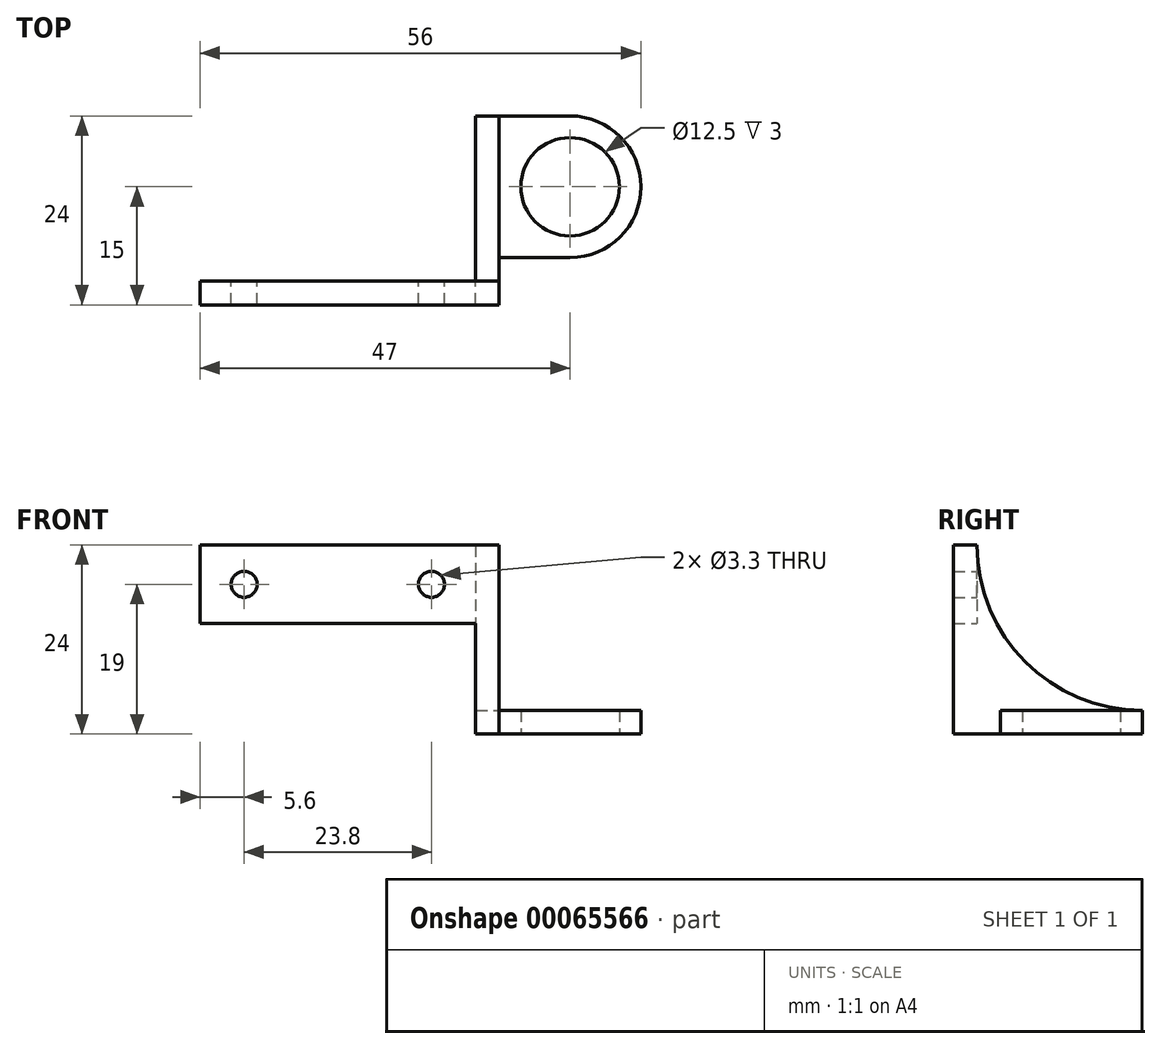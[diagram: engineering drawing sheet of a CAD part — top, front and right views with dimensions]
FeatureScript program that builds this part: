
annotation { "Feature Type Name" : "Feature", "Feature Type Description" : "" }
export const myFeature = defineFeature(function(context is Context, id is Id, definition is map)
    precondition{}
    {
        {
            var Q0;
            Q0=qCreatedBy(makeId("Front.planeOp"),FACE);
            var sketch = newSketch(context, id + "F0", { "sketchPlane" : qUnion([Q0])});
            skLineSegment(sketch, "E0.bottom", {"start": v(-17.5, 5) * mm, "end": v(17.5, 5) * mm});
            skLineSegment(sketch, "E0.top", {"start": v(-17.5, -5) * mm, "end": v(17.5, -5) * mm});
            skLineSegment(sketch, "E0.left", {"start": v(-17.5, 5) * mm, "end": v(-17.5, -5) * mm});
            skLineSegment(sketch, "E0.right", {"start": v(17.5, 5) * mm, "end": v(17.5, -5) * mm});
            skCircle(sketch, "E1", {"center": v(-11.9, 0) * mm, "radius": 1.65 * mm});
            skCircle(sketch, "E2", {"center": v(11.9, 0) * mm, "radius": 1.65 * mm});
            skSolve(sketch);
        }
        {
            var Q0;
            Q0=makeQuery(id+"F0.imprint","IMPRINT",FACE,{"disambiguationData":[TD([[makeQuery(id+"F0.imprint","IMPRINT",EDGE,{"derivedFrom":sQuery(id+"F0.wireOp",EDGE,"E0.bottom")}),-1.0]])]});
            extrude(context, id + "F1", {"entities" : qUnion([Q0]), "depth" : 3 * mm});
        }
        {
            var Q0;
            Q0=makeQuery(id+"F1.opExtrude","SWEPT_FACE",FACE,{"disambiguationData":[OSD([sQuery(id+"F0.wireOp",EDGE,"E0.right")])]});
            var sketch = newSketch(context, id + "F2", { "sketchPlane" : qUnion([Q0])});
            skLineSegment(sketch, "E3.bottom", {"start": v(-3, 5) * mm, "end": v(21, 5) * mm});
            skLineSegment(sketch, "E3.top", {"start": v(-3, -19) * mm, "end": v(21, -19) * mm});
            skLineSegment(sketch, "E3.left", {"start": v(-3, 5) * mm, "end": v(-3, -19) * mm});
            skLineSegment(sketch, "E3.right", {"start": v(21, 5) * mm, "end": v(21, -19) * mm});
            skSolve(sketch);
        }
        {
            var Q0;
            Q0 = qSketchRegion(id + "F2", true);
            extrude(context, id + "F3", {"entities" : qUnion([Q0]), "operationType" : NewBodyOperationType.ADD, "depth" : 3 * mm});
        }
        {
            var Q0;
            Q0=makeQuery(id+"F3.opExtrude","SWEPT_FACE",FACE,{"disambiguationData":[OSD([sQuery(id+"F2.wireOp",EDGE,"E3.top")])]});
            var sketch = newSketch(context, id + "F4", { "sketchPlane" : qUnion([Q0])});
            skArc(sketch, "E4", {"start": v(29.5, -21) * mm, "mid": v(38.5, -12) * mm, "end": v(29.5, -3) * mm});
            skCircle(sketch, "E5", {"center": v(29.5, -12) * mm, "radius": 6.25 * mm});
            skLineSegment(sketch, "E6", {"start": v(20.5, -21) * mm, "end": v(29.5, -21) * mm});
            skLineSegment(sketch, "E7", {"start": v(20.5, -3) * mm, "end": v(29.5, -3) * mm});
            skSolve(sketch);
        }
        {
            var Q0;
            Q0=makeQuery(id+"F4.imprint","IMPRINT",FACE,{"disambiguationData":[TD([[makeQuery(id+"F4.imprint","IMPRINT",EDGE,{"derivedFrom":sQuery(id+"F4.wireOp",EDGE,"E4")}),1.0]])]});
            extrude(context, id + "F5", {"entities" : qUnion([Q0]), "operationType" : NewBodyOperationType.ADD, "oppositeDirection" : true, "depth" : 3 * mm});
        }
        {
            var Q0;
            Q0=makeQuery(id+"F3.opExtrude","CAP_FACE",FACE,{"disambiguationData":[OSD([sQuery(id+"F2.wireOp",EDGE,"E3.bottom"),sQuery(id+"F2.wireOp",EDGE,"E3.top"),sQuery(id+"F2.wireOp",EDGE,"E3.left"),sQuery(id+"F2.wireOp",EDGE,"E3.right")])],"isStart":false});
            var sketch = newSketch(context, id + "F6", { "sketchPlane" : qUnion([Q0])});
            skCircle(sketch, "E8", {"center": v(21, 5) * mm, "radius": 21 * mm});
            skSolve(sketch);
        }
        {
            var Q0;
            Q0 = qSketchRegion(id + "F6", true);
            extrude(context, id + "F7", {"entities" : qUnion([Q0]), "operationType" : NewBodyOperationType.REMOVE, "oppositeDirection" : true, "depth" : 3 * mm});
        }
    });
